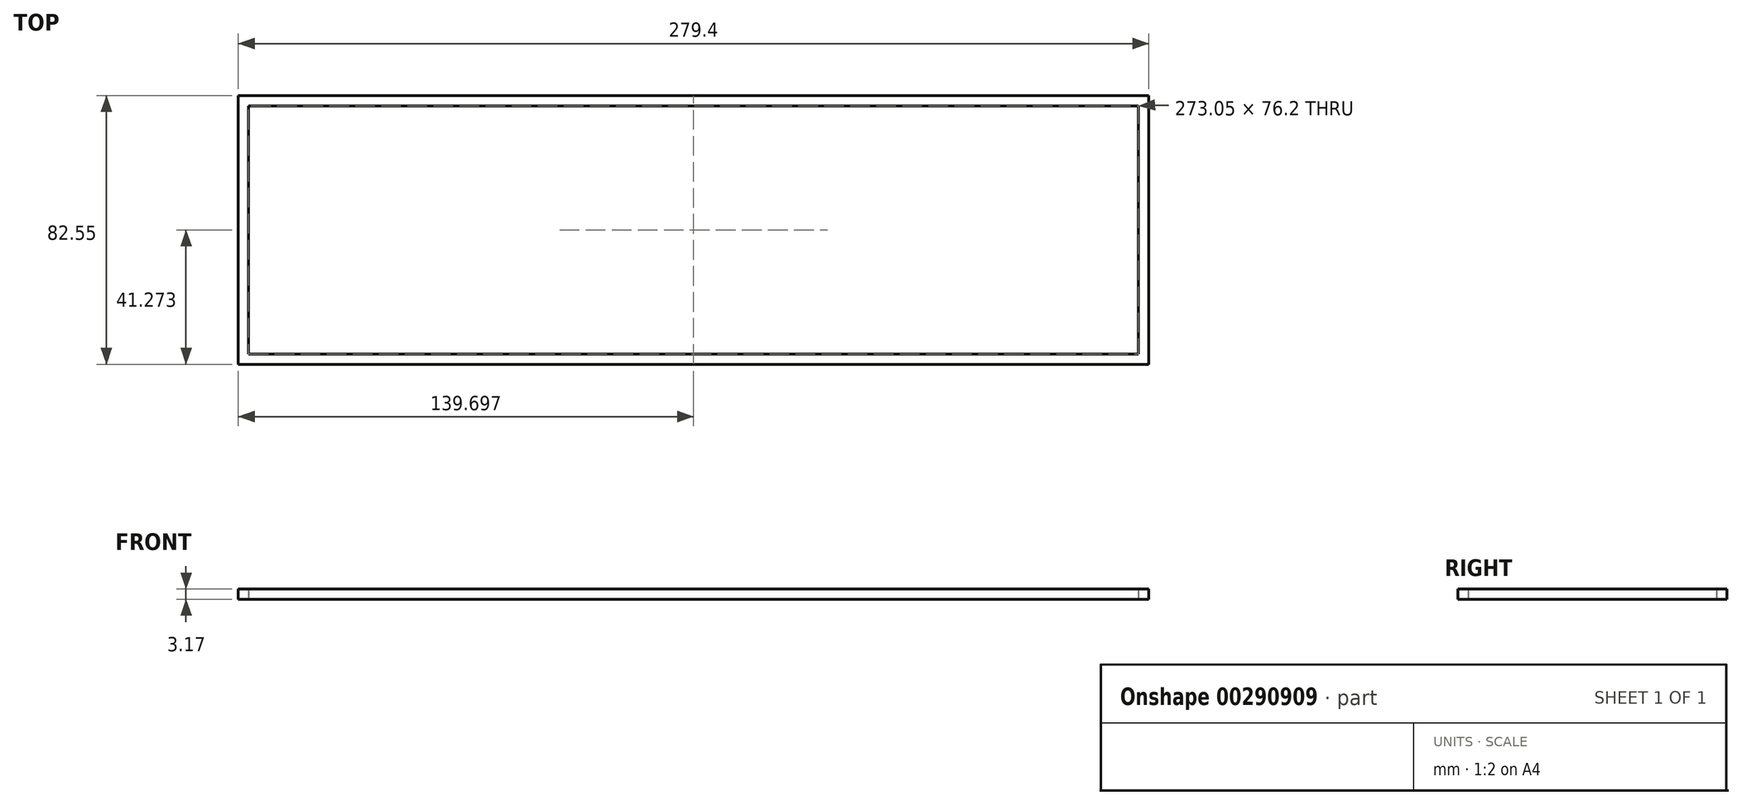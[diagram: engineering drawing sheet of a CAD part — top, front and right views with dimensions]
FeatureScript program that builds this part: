
annotation { "Feature Type Name" : "Feature", "Feature Type Description" : "" }
export const myFeature = defineFeature(function(context is Context, id is Id, definition is map)
    precondition{}
    {
        {
            var Q0;
            Q0=qCreatedBy(makeId("Top.planeOp"),FACE);
            var sketch = newSketch(context, id + "F0", { "sketchPlane" : qUnion([Q0])});
            skLineSegment(sketch, "E0.bottom", {"start": v(-144.23, 44.64) * mm, "end": v(135.17, 44.64) * mm});
            skLineSegment(sketch, "E0.top", {"start": v(-144.23, -37.91) * mm, "end": v(135.17, -37.91) * mm});
            skLineSegment(sketch, "E0.left", {"start": v(-144.23, 44.64) * mm, "end": v(-144.23, -37.91) * mm});
            skLineSegment(sketch, "E0.right", {"start": v(135.17, 44.64) * mm, "end": v(135.17, -37.91) * mm});
            skLineSegment(sketch, "E1.0", {"start": v(-141.06, 41.46) * mm, "end": v(132, 41.46) * mm});
            skLineSegment(sketch, "E1.1", {"start": v(-141.06, 41.46) * mm, "end": v(-141.06, -34.74) * mm});
            skLineSegment(sketch, "E1.2", {"start": v(-141.06, -34.74) * mm, "end": v(132, -34.74) * mm});
            skLineSegment(sketch, "E1.3", {"start": v(132, 41.46) * mm, "end": v(132, -34.74) * mm});
            skLineSegment(sketch, "E2", {"start": v(-4.53, 41.46) * mm, "end": v(-4.53, -34.74) * mm, "construction": true});
            skSolve(sketch);
        }
        {
            var Q0;
            Q0=makeQuery(id+"F0.imprint","IMPRINT",FACE,{"disambiguationData":[TD([[makeQuery(id+"F0.imprint","IMPRINT",EDGE,{"derivedFrom":sQuery(id+"F0.wireOp",EDGE,"E0.bottom")}),-1.0]])]});
            extrude(context, id + "F1", {"entities" : qUnion([Q0]), "depth" : 3.17 * mm});
        }
    });
